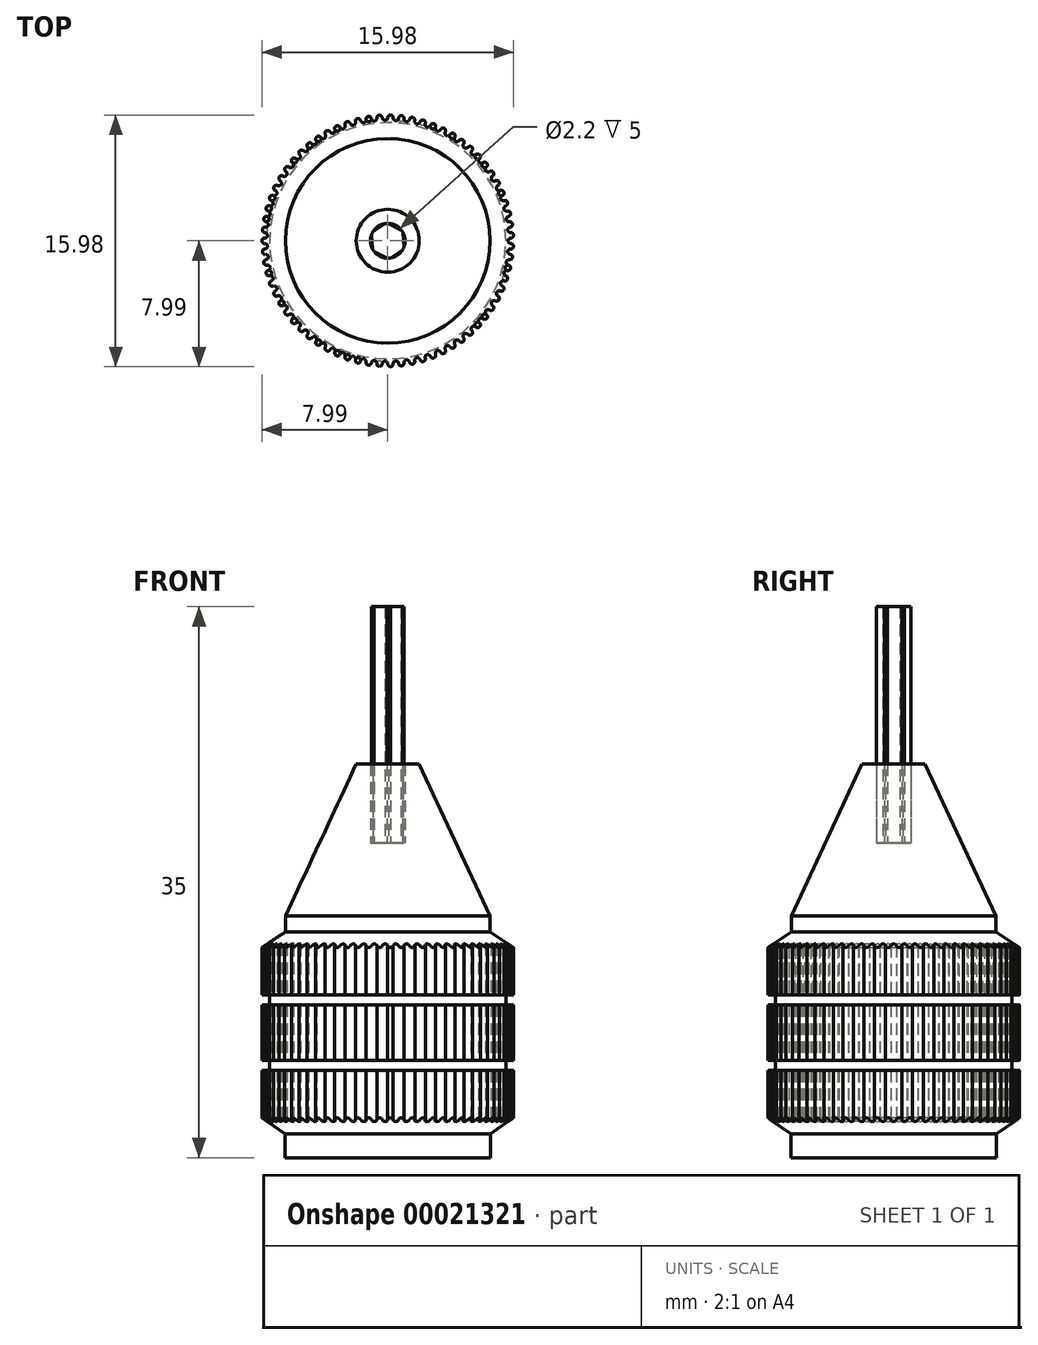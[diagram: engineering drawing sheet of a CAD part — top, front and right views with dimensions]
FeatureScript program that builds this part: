
annotation { "Feature Type Name" : "Feature", "Feature Type Description" : "" }
export const myFeature = defineFeature(function(context is Context, id is Id, definition is map)
    precondition{}
    {
        {
            var Q0;
            Q0=qCreatedBy(makeId("Front.planeOp"),FACE);
            var sketch = newSketch(context, id + "F0", { "sketchPlane" : qUnion([Q0])});
            skLineSegment(sketch, "E0", {"start": v(0, 0) * mm, "end": v(0, 25) * mm, "construction": true});
            skLineSegment(sketch, "E1", {"start": v(0, 0) * mm, "end": v(6.53, 0) * mm});
            skLineSegment(sketch, "E2", {"start": v(6.53, 0) * mm, "end": v(6.53, 1.5) * mm});
            skLineSegment(sketch, "E3", {"start": v(6.53, 1.5) * mm, "end": v(8, 2.54) * mm});
            skLineSegment(sketch, "E4", {"start": v(8, 2.54) * mm, "end": v(8, 13.34) * mm, "construction": true});
            skLineSegment(sketch, "E5", {"start": v(8, 13.34) * mm, "end": v(6.5, 14.34) * mm});
            skLineSegment(sketch, "E6", {"start": v(6.5, 14.34) * mm, "end": v(6.5, 15.34) * mm});
            skLineSegment(sketch, "E7", {"start": v(2, 25) * mm, "end": v(6.5, 15.34) * mm});
            skLineSegment(sketch, "E8", {"start": v(1.1, 25) * mm, "end": v(1.1, 20) * mm});
            skLineSegment(sketch, "E9", {"start": v(1.1, 20) * mm, "end": v(0, 20) * mm});
            skLineSegment(sketch, "E10", {"start": v(1.1, 25) * mm, "end": v(2, 25) * mm});
            skLineSegment(sketch, "E11", {"start": v(8, 13.34) * mm, "end": v(8, 10.34) * mm});
            skLineSegment(sketch, "E12", {"start": v(8, 10.34) * mm, "end": v(7.5, 10.34) * mm});
            skLineSegment(sketch, "E13", {"start": v(7.5, 10.34) * mm, "end": v(7.5, 9.69) * mm});
            skLineSegment(sketch, "E14", {"start": v(7.5, 9.69) * mm, "end": v(8, 9.69) * mm});
            skLineSegment(sketch, "E15", {"start": v(8, 9.69) * mm, "end": v(8, 6.19) * mm});
            skLineSegment(sketch, "E16", {"start": v(8, 6.19) * mm, "end": v(7.5, 6.19) * mm});
            skLineSegment(sketch, "E17", {"start": v(7.5, 6.19) * mm, "end": v(7.5, 5.54) * mm});
            skLineSegment(sketch, "E18", {"start": v(7.5, 5.54) * mm, "end": v(8, 5.54) * mm});
            skLineSegment(sketch, "E19", {"start": v(8, 5.54) * mm, "end": v(8, 2.54) * mm});
            skLineSegment(sketch, "E20", {"start": v(0, 20) * mm, "end": v(0, 0) * mm});
            skSolve(sketch);
        }
        {
            var Q0;
            Q0=qSketchRegion(id+"F0",true);
            var Q1;
            Q1=sQuery(id+"F0.wireOp",EDGE,"E7");
            var Q2;
            Q2=sQuery(id+"F0.wireOp",EDGE,"E5");
            var Q3;
            Q3=sQuery(id+"F0.wireOp",EDGE,"E6");
            var Q4;
            Q4=sQuery(id+"F0.wireOp",EDGE,"E3");
            var Q5;
            Q5=sQuery(id+"F0.wireOp",EDGE,"E2");
            var Q6;
            Q6=sQuery(id+"F0.wireOp",EDGE,"E1");
            var Q7;
            Q7=sQuery(id+"F0.wireOp",EDGE,"E8");
            var Q8;
            Q8=sQuery(id+"F0.wireOp",EDGE,"E9");
            var Q9;
            Q9=sQuery(id+"F0.wireOp",EDGE,"E10");
            var Q10;
            Q10=sQuery(id+"F0.wireOp",EDGE,"E13");
            var Q11;
            Q11=sQuery(id+"F0.wireOp",EDGE,"E12");
            var Q12;
            Q12=sQuery(id+"F0.wireOp",EDGE,"E14");
            var Q13;
            Q13=sQuery(id+"F0.wireOp",EDGE,"E11");
            var Q14;
            Q14=sQuery(id+"F0.wireOp",EDGE,"E15");
            var Q15;
            Q15=sQuery(id+"F0.wireOp",EDGE,"E17");
            var Q16;
            Q16=sQuery(id+"F0.wireOp",EDGE,"E16");
            var Q17;
            Q17=sQuery(id+"F0.wireOp",EDGE,"E18");
            var Q18;
            Q18=sQuery(id+"F0.wireOp",EDGE,"E19");
            var Q19;
            Q19=sQuery(id+"F0.wireOp",EDGE,"E0");
            revolve(context, id + "F1", {"entities" : qUnion([Q0]), "surfaceEntities" : qUnion([Q1, Q2, Q3, Q4, Q5, Q6, Q7, Q8, Q9, Q10, Q11, Q12, Q13, Q14, Q15, Q16, Q17, Q18]), "axis" : qUnion([Q19]), "revolveType" : RevolveType.ONE_DIRECTION, "angle" : 360 * degree});
        }
        {
            var Q0;
            Q0=makeQuery(id+"F1.opRevolve","SWEPT_FACE",FACE,{"disambiguationData":[OSD([sQuery(id+"F0.wireOp",EDGE,"E10")])]});
            var sketch = newSketch(context, id + "F2", { "sketchPlane" : qUnion([Q0])});
            skCircle(sketch, "E21.cCircle", {"center": v(0, 0) * mm, "radius": 1 * mm, "construction": true});
            skLineSegment(sketch, "E21.0", {"start": v(1.03, -0.52) * mm, "end": v(0.06, -1.15) * mm});
            skLineSegment(sketch, "E21.1", {"start": v(0.06, -1.15) * mm, "end": v(-0.97, -0.63) * mm});
            skLineSegment(sketch, "E21.2", {"start": v(-0.97, -0.63) * mm, "end": v(-1.03, 0.52) * mm});
            skLineSegment(sketch, "E21.3", {"start": v(-1.03, 0.52) * mm, "end": v(-0.06, 1.15) * mm});
            skLineSegment(sketch, "E21.4", {"start": v(-0.06, 1.15) * mm, "end": v(0.97, 0.63) * mm});
            skLineSegment(sketch, "E21.5", {"start": v(0.97, 0.63) * mm, "end": v(1.03, -0.52) * mm});
            skPoint(sketch, "E21.0.midPoint", {"position": v(0.55, -0.84) * mm});
            skSolve(sketch);
        }
        {
            var Q0;
            {var subQ0=makeQuery(id+"F1.opRevolve","SWEPT_EDGE",EDGE,{"disambiguationData":[OSD([sQuery(id+"F0.wireOp",VERTEX,"E10.start")])]});var subQ7=sQuery(id+"F2.wireOp",EDGE,"E21.0");var subQ13=makeQuery(id+"F2.imprint","INTERSECT",VERTEX,{"disambiguationData":[OD(0.0)],"derivedFrom":[subQ0,subQ7]});Q0=makeQuery(id+"F2.imprint","IMPRINT",FACE,{"disambiguationData":[TD([[makeQuery(id+"F2.imprint","IMPRINT",EDGE,{"disambiguationData":[TD([[subQ13,-1.0]])],"derivedFrom":subQ7}),-1.0]])]});}
            extrude(context, id + "F3", {"entities" : qUnion([Q0]), "depth" : 10 * mm, "hasSecondDirection" : true, "secondDirectionOppositeDirection" : true, "secondDirectionDepth" : 5 * mm});
        }
        {
            var Q0;
            Q0=qCreatedBy(makeId("Top.planeOp"),FACE);
            var sketch = newSketch(context, id + "F4", { "sketchPlane" : qUnion([Q0])});
            skLineSegment(sketch, "E22", {"start": v(0, 7.82) * mm, "end": v(0, 0) * mm, "construction": true});
            skLineSegment(sketch, "E23", {"start": v(0, 0) * mm, "end": v(0.7, 7.79) * mm, "construction": true});
            skArc(sketch, "E24", {"start": v(0.35, 7.81) * mm, "mid": v(0.18, 8) * mm, "end": v(0, 7.82) * mm});
            skArc(sketch, "E25", {"start": v(0.35, 7.81) * mm, "mid": v(0.5, 7.63) * mm, "end": v(0.7, 7.79) * mm});
            skArc(sketch, "E26", {"start": v(0.7, 7.79) * mm, "mid": v(0.35, 7.81) * mm, "end": v(0, 7.82) * mm, "construction": true});
            skCircle(sketch, "E27", {"center": v(0, 0) * mm, "radius": 8.29 * mm});
            skCircle(sketch, "E28", {"center": v(0, 0) * mm, "radius": 8 * mm, "construction": true});
            skArc(sketch, "E29.1.0", {"start": v(1.03, 7.75) * mm, "mid": v(1.18, 7.56) * mm, "end": v(1.38, 7.7) * mm});
            skArc(sketch, "E29.1.1", {"start": v(1.03, 7.75) * mm, "mid": v(0.88, 7.94) * mm, "end": v(0.7, 7.79) * mm});
            skArc(sketch, "E29.2.0", {"start": v(1.72, 7.63) * mm, "mid": v(1.84, 7.42) * mm, "end": v(2.05, 7.54) * mm});
            skArc(sketch, "E29.2.1", {"start": v(1.72, 7.63) * mm, "mid": v(1.58, 7.84) * mm, "end": v(1.38, 7.7) * mm});
            skArc(sketch, "E29.3.0", {"start": v(2.38, 7.45) * mm, "mid": v(2.5, 7.23) * mm, "end": v(2.71, 7.33) * mm});
            skArc(sketch, "E29.3.1", {"start": v(2.38, 7.45) * mm, "mid": v(2.27, 7.67) * mm, "end": v(2.05, 7.54) * mm});
            skArc(sketch, "E29.4.0", {"start": v(3.03, 7.2) * mm, "mid": v(3.12, 6.98) * mm, "end": v(3.35, 7.07) * mm});
            skArc(sketch, "E29.4.1", {"start": v(3.03, 7.2) * mm, "mid": v(2.94, 7.43) * mm, "end": v(2.71, 7.33) * mm});
            skArc(sketch, "E29.5.0", {"start": v(3.66, 6.91) * mm, "mid": v(3.73, 6.68) * mm, "end": v(3.96, 6.74) * mm});
            skArc(sketch, "E29.5.1", {"start": v(3.66, 6.91) * mm, "mid": v(3.58, 7.15) * mm, "end": v(3.35, 7.07) * mm});
            skArc(sketch, "E29.6.0", {"start": v(4.25, 6.56) * mm, "mid": v(4.3, 6.32) * mm, "end": v(4.54, 6.37) * mm});
            skArc(sketch, "E29.6.1", {"start": v(4.25, 6.56) * mm, "mid": v(4.2, 6.8) * mm, "end": v(3.96, 6.74) * mm});
            skArc(sketch, "E29.7.0", {"start": v(4.82, 6.16) * mm, "mid": v(4.84, 5.92) * mm, "end": v(5.08, 5.94) * mm});
            skArc(sketch, "E29.7.1", {"start": v(4.82, 6.16) * mm, "mid": v(4.78, 6.4) * mm, "end": v(4.54, 6.37) * mm});
            skArc(sketch, "E29.8.0", {"start": v(5.34, 5.7) * mm, "mid": v(5.35, 5.47) * mm, "end": v(5.59, 5.47) * mm});
            skArc(sketch, "E29.8.1", {"start": v(5.34, 5.7) * mm, "mid": v(5.33, 5.96) * mm, "end": v(5.08, 5.94) * mm});
            skArc(sketch, "E29.9.0", {"start": v(5.83, 5.21) * mm, "mid": v(5.8, 4.97) * mm, "end": v(6.05, 4.95) * mm});
            skArc(sketch, "E29.9.1", {"start": v(5.83, 5.21) * mm, "mid": v(5.84, 5.46) * mm, "end": v(5.59, 5.47) * mm});
            skArc(sketch, "E29.10.0", {"start": v(6.26, 4.68) * mm, "mid": v(6.23, 4.44) * mm, "end": v(6.46, 4.4) * mm});
            skArc(sketch, "E29.10.1", {"start": v(6.26, 4.68) * mm, "mid": v(6.3, 4.92) * mm, "end": v(6.05, 4.95) * mm});
            skArc(sketch, "E29.11.0", {"start": v(6.65, 4.1) * mm, "mid": v(6.6, 3.87) * mm, "end": v(6.83, 3.8) * mm});
            skArc(sketch, "E29.11.1", {"start": v(6.65, 4.1) * mm, "mid": v(6.7, 4.35) * mm, "end": v(6.46, 4.4) * mm});
            skArc(sketch, "E29.12.0", {"start": v(6.99, 3.5) * mm, "mid": v(6.91, 3.27) * mm, "end": v(7.14, 3.2) * mm});
            skArc(sketch, "E29.12.1", {"start": v(6.99, 3.5) * mm, "mid": v(7.07, 3.74) * mm, "end": v(6.83, 3.8) * mm});
            skArc(sketch, "E29.13.0", {"start": v(7.27, 2.87) * mm, "mid": v(7.17, 2.65) * mm, "end": v(7.4, 2.55) * mm});
            skArc(sketch, "E29.13.1", {"start": v(7.27, 2.87) * mm, "mid": v(7.37, 3.1) * mm, "end": v(7.14, 3.2) * mm});
            skArc(sketch, "E29.14.0", {"start": v(7.5, 2.22) * mm, "mid": v(7.38, 2) * mm, "end": v(7.59, 1.88) * mm});
            skArc(sketch, "E29.14.1", {"start": v(7.5, 2.22) * mm, "mid": v(7.61, 2.44) * mm, "end": v(7.4, 2.55) * mm});
            skArc(sketch, "E29.15.0", {"start": v(7.66, 1.55) * mm, "mid": v(7.53, 1.35) * mm, "end": v(7.73, 1.2) * mm});
            skArc(sketch, "E29.15.1", {"start": v(7.66, 1.55) * mm, "mid": v(7.8, 1.75) * mm, "end": v(7.59, 1.88) * mm});
            skArc(sketch, "E29.16.0", {"start": v(7.77, 0.86) * mm, "mid": v(7.62, 0.68) * mm, "end": v(7.8, 0.52) * mm});
            skArc(sketch, "E29.16.1", {"start": v(7.77, 0.86) * mm, "mid": v(7.92, 1.06) * mm, "end": v(7.73, 1.2) * mm});
            skArc(sketch, "E29.17.0", {"start": v(7.82, 0.17) * mm, "mid": v(7.65, 0) * mm, "end": v(7.82, -0.17) * mm});
            skArc(sketch, "E29.17.1", {"start": v(7.82, 0.17) * mm, "mid": v(7.99, 0.35) * mm, "end": v(7.8, 0.52) * mm});
            skArc(sketch, "E29.18.0", {"start": v(7.8, -0.52) * mm, "mid": v(7.62, -0.68) * mm, "end": v(7.77, -0.86) * mm});
            skArc(sketch, "E29.18.1", {"start": v(7.8, -0.52) * mm, "mid": v(7.99, -0.35) * mm, "end": v(7.82, -0.17) * mm});
            skArc(sketch, "E29.19.0", {"start": v(7.73, -1.2) * mm, "mid": v(7.53, -1.35) * mm, "end": v(7.66, -1.55) * mm});
            skArc(sketch, "E29.19.1", {"start": v(7.73, -1.2) * mm, "mid": v(7.92, -1.06) * mm, "end": v(7.77, -0.86) * mm});
            skArc(sketch, "E29.20.0", {"start": v(7.59, -1.88) * mm, "mid": v(7.38, -2) * mm, "end": v(7.5, -2.22) * mm});
            skArc(sketch, "E29.20.1", {"start": v(7.59, -1.88) * mm, "mid": v(7.8, -1.75) * mm, "end": v(7.66, -1.55) * mm});
            skArc(sketch, "E29.21.0", {"start": v(7.4, -2.55) * mm, "mid": v(7.17, -2.65) * mm, "end": v(7.27, -2.87) * mm});
            skArc(sketch, "E29.21.1", {"start": v(7.4, -2.55) * mm, "mid": v(7.61, -2.44) * mm, "end": v(7.5, -2.22) * mm});
            skArc(sketch, "E29.22.0", {"start": v(7.14, -3.2) * mm, "mid": v(6.91, -3.27) * mm, "end": v(6.99, -3.5) * mm});
            skArc(sketch, "E29.22.1", {"start": v(7.14, -3.2) * mm, "mid": v(7.37, -3.1) * mm, "end": v(7.27, -2.87) * mm});
            skArc(sketch, "E29.23.0", {"start": v(6.83, -3.8) * mm, "mid": v(6.6, -3.87) * mm, "end": v(6.65, -4.1) * mm});
            skArc(sketch, "E29.23.1", {"start": v(6.83, -3.8) * mm, "mid": v(7.07, -3.74) * mm, "end": v(6.99, -3.5) * mm});
            skArc(sketch, "E29.24.0", {"start": v(6.46, -4.4) * mm, "mid": v(6.23, -4.44) * mm, "end": v(6.26, -4.68) * mm});
            skArc(sketch, "E29.24.1", {"start": v(6.46, -4.4) * mm, "mid": v(6.7, -4.35) * mm, "end": v(6.65, -4.1) * mm});
            skArc(sketch, "E29.25.0", {"start": v(6.05, -4.95) * mm, "mid": v(5.8, -4.97) * mm, "end": v(5.83, -5.21) * mm});
            skArc(sketch, "E29.25.1", {"start": v(6.05, -4.95) * mm, "mid": v(6.3, -4.92) * mm, "end": v(6.26, -4.68) * mm});
            skArc(sketch, "E29.26.0", {"start": v(5.59, -5.47) * mm, "mid": v(5.35, -5.47) * mm, "end": v(5.34, -5.7) * mm});
            skArc(sketch, "E29.26.1", {"start": v(5.59, -5.47) * mm, "mid": v(5.84, -5.46) * mm, "end": v(5.83, -5.21) * mm});
            skArc(sketch, "E29.27.0", {"start": v(5.08, -5.94) * mm, "mid": v(4.84, -5.92) * mm, "end": v(4.82, -6.16) * mm});
            skArc(sketch, "E29.27.1", {"start": v(5.08, -5.94) * mm, "mid": v(5.33, -5.96) * mm, "end": v(5.34, -5.7) * mm});
            skArc(sketch, "E29.28.0", {"start": v(4.54, -6.37) * mm, "mid": v(4.3, -6.32) * mm, "end": v(4.25, -6.56) * mm});
            skArc(sketch, "E29.28.1", {"start": v(4.54, -6.37) * mm, "mid": v(4.78, -6.4) * mm, "end": v(4.82, -6.16) * mm});
            skArc(sketch, "E29.29.0", {"start": v(3.96, -6.74) * mm, "mid": v(3.73, -6.68) * mm, "end": v(3.66, -6.91) * mm});
            skArc(sketch, "E29.29.1", {"start": v(3.96, -6.74) * mm, "mid": v(4.2, -6.8) * mm, "end": v(4.25, -6.56) * mm});
            skArc(sketch, "E29.30.0", {"start": v(3.35, -7.07) * mm, "mid": v(3.12, -6.98) * mm, "end": v(3.03, -7.2) * mm});
            skArc(sketch, "E29.30.1", {"start": v(3.35, -7.07) * mm, "mid": v(3.58, -7.15) * mm, "end": v(3.66, -6.91) * mm});
            skArc(sketch, "E29.31.0", {"start": v(2.71, -7.33) * mm, "mid": v(2.5, -7.23) * mm, "end": v(2.38, -7.45) * mm});
            skArc(sketch, "E29.31.1", {"start": v(2.71, -7.33) * mm, "mid": v(2.94, -7.43) * mm, "end": v(3.03, -7.2) * mm});
            skArc(sketch, "E29.32.0", {"start": v(2.05, -7.54) * mm, "mid": v(1.84, -7.42) * mm, "end": v(1.72, -7.63) * mm});
            skArc(sketch, "E29.32.1", {"start": v(2.05, -7.54) * mm, "mid": v(2.27, -7.67) * mm, "end": v(2.38, -7.45) * mm});
            skArc(sketch, "E29.33.0", {"start": v(1.38, -7.7) * mm, "mid": v(1.18, -7.56) * mm, "end": v(1.03, -7.75) * mm});
            skArc(sketch, "E29.33.1", {"start": v(1.38, -7.7) * mm, "mid": v(1.58, -7.84) * mm, "end": v(1.72, -7.63) * mm});
            skArc(sketch, "E29.34.0", {"start": v(0.7, -7.79) * mm, "mid": v(0.5, -7.63) * mm, "end": v(0.35, -7.81) * mm});
            skArc(sketch, "E29.34.1", {"start": v(0.7, -7.79) * mm, "mid": v(0.88, -7.94) * mm, "end": v(1.03, -7.75) * mm});
            skArc(sketch, "E29.35.0", {"start": v(0, -7.82) * mm, "mid": v(-0.17, -7.65) * mm, "end": v(-0.35, -7.81) * mm});
            skArc(sketch, "E29.35.1", {"start": v(0, -7.82) * mm, "mid": v(0.18, -8) * mm, "end": v(0.35, -7.81) * mm});
            skArc(sketch, "E29.36.0", {"start": v(-0.7, -7.79) * mm, "mid": v(-0.84, -7.6) * mm, "end": v(-1.03, -7.75) * mm});
            skArc(sketch, "E29.36.1", {"start": v(-0.7, -7.79) * mm, "mid": v(-0.53, -7.98) * mm, "end": v(-0.35, -7.81) * mm});
            skArc(sketch, "E29.37.0", {"start": v(-1.38, -7.7) * mm, "mid": v(-1.51, -7.5) * mm, "end": v(-1.72, -7.63) * mm});
            skArc(sketch, "E29.37.1", {"start": v(-1.38, -7.7) * mm, "mid": v(-1.23, -7.9) * mm, "end": v(-1.03, -7.75) * mm});
            skArc(sketch, "E29.38.0", {"start": v(-2.05, -7.54) * mm, "mid": v(-2.17, -7.33) * mm, "end": v(-2.38, -7.45) * mm});
            skArc(sketch, "E29.38.1", {"start": v(-2.05, -7.54) * mm, "mid": v(-1.93, -7.76) * mm, "end": v(-1.72, -7.63) * mm});
            skArc(sketch, "E29.39.0", {"start": v(-2.71, -7.33) * mm, "mid": v(-2.8, -7.11) * mm, "end": v(-3.03, -7.2) * mm});
            skArc(sketch, "E29.39.1", {"start": v(-2.71, -7.33) * mm, "mid": v(-2.6, -7.56) * mm, "end": v(-2.38, -7.45) * mm});
            skArc(sketch, "E29.40.0", {"start": v(-3.35, -7.07) * mm, "mid": v(-3.43, -6.84) * mm, "end": v(-3.66, -6.91) * mm});
            skArc(sketch, "E29.40.1", {"start": v(-3.35, -7.07) * mm, "mid": v(-3.26, -7.3) * mm, "end": v(-3.03, -7.2) * mm});
            skArc(sketch, "E29.41.0", {"start": v(-3.96, -6.74) * mm, "mid": v(-4.02, -6.5) * mm, "end": v(-4.25, -6.56) * mm});
            skArc(sketch, "E29.41.1", {"start": v(-3.96, -6.74) * mm, "mid": v(-3.9, -6.98) * mm, "end": v(-3.66, -6.91) * mm});
            skArc(sketch, "E29.42.0", {"start": v(-4.54, -6.37) * mm, "mid": v(-4.58, -6.13) * mm, "end": v(-4.82, -6.16) * mm});
            skArc(sketch, "E29.42.1", {"start": v(-4.54, -6.37) * mm, "mid": v(-4.5, -6.6) * mm, "end": v(-4.25, -6.56) * mm});
            skArc(sketch, "E29.43.0", {"start": v(-5.08, -5.94) * mm, "mid": v(-5.1, -5.7) * mm, "end": v(-5.34, -5.7) * mm});
            skArc(sketch, "E29.43.1", {"start": v(-5.08, -5.94) * mm, "mid": v(-5.06, -6.19) * mm, "end": v(-4.82, -6.16) * mm});
            skArc(sketch, "E29.44.0", {"start": v(-5.59, -5.47) * mm, "mid": v(-5.58, -5.23) * mm, "end": v(-5.83, -5.21) * mm});
            skArc(sketch, "E29.44.1", {"start": v(-5.59, -5.47) * mm, "mid": v(-5.59, -5.71) * mm, "end": v(-5.34, -5.7) * mm});
            skArc(sketch, "E29.45.0", {"start": v(-6.05, -4.95) * mm, "mid": v(-6.02, -4.71) * mm, "end": v(-6.26, -4.68) * mm});
            skArc(sketch, "E29.45.1", {"start": v(-6.05, -4.95) * mm, "mid": v(-6.07, -5.2) * mm, "end": v(-5.83, -5.21) * mm});
            skArc(sketch, "E29.46.0", {"start": v(-6.46, -4.4) * mm, "mid": v(-6.42, -4.16) * mm, "end": v(-6.65, -4.1) * mm});
            skArc(sketch, "E29.46.1", {"start": v(-6.46, -4.4) * mm, "mid": v(-6.5, -4.64) * mm, "end": v(-6.26, -4.68) * mm});
            skArc(sketch, "E29.47.0", {"start": v(-6.83, -3.8) * mm, "mid": v(-6.76, -3.58) * mm, "end": v(-6.99, -3.5) * mm});
            skArc(sketch, "E29.47.1", {"start": v(-6.83, -3.8) * mm, "mid": v(-6.9, -4.05) * mm, "end": v(-6.65, -4.1) * mm});
            skArc(sketch, "E29.48.0", {"start": v(-7.14, -3.2) * mm, "mid": v(-7.05, -2.97) * mm, "end": v(-7.27, -2.87) * mm});
            skArc(sketch, "E29.48.1", {"start": v(-7.14, -3.2) * mm, "mid": v(-7.22, -3.42) * mm, "end": v(-6.99, -3.5) * mm});
            skArc(sketch, "E29.49.0", {"start": v(-7.4, -2.55) * mm, "mid": v(-7.28, -2.33) * mm, "end": v(-7.5, -2.22) * mm});
            skArc(sketch, "E29.49.1", {"start": v(-7.4, -2.55) * mm, "mid": v(-7.5, -2.77) * mm, "end": v(-7.27, -2.87) * mm});
            skArc(sketch, "E29.50.0", {"start": v(-7.59, -1.88) * mm, "mid": v(-7.46, -1.68) * mm, "end": v(-7.66, -1.55) * mm});
            skArc(sketch, "E29.50.1", {"start": v(-7.59, -1.88) * mm, "mid": v(-7.71, -2.1) * mm, "end": v(-7.5, -2.22) * mm});
            skArc(sketch, "E29.51.0", {"start": v(-7.73, -1.2) * mm, "mid": v(-7.58, -1.01) * mm, "end": v(-7.77, -0.86) * mm});
            skArc(sketch, "E29.51.1", {"start": v(-7.73, -1.2) * mm, "mid": v(-7.87, -1.4) * mm, "end": v(-7.66, -1.55) * mm});
            skArc(sketch, "E29.52.0", {"start": v(-7.8, -0.52) * mm, "mid": v(-7.64, -0.34) * mm, "end": v(-7.82, -0.17) * mm});
            skArc(sketch, "E29.52.1", {"start": v(-7.8, -0.52) * mm, "mid": v(-7.96, -0.7) * mm, "end": v(-7.77, -0.86) * mm});
            skArc(sketch, "E29.53.0", {"start": v(-7.82, 0.17) * mm, "mid": v(-7.64, 0.34) * mm, "end": v(-7.8, 0.52) * mm});
            skArc(sketch, "E29.53.1", {"start": v(-7.82, 0.17) * mm, "mid": v(-8, 0) * mm, "end": v(-7.82, -0.17) * mm});
            skArc(sketch, "E29.54.0", {"start": v(-7.77, 0.86) * mm, "mid": v(-7.58, 1.01) * mm, "end": v(-7.73, 1.2) * mm});
            skArc(sketch, "E29.54.1", {"start": v(-7.77, 0.86) * mm, "mid": v(-7.96, 0.7) * mm, "end": v(-7.8, 0.52) * mm});
            skArc(sketch, "E29.55.0", {"start": v(-7.66, 1.55) * mm, "mid": v(-7.46, 1.68) * mm, "end": v(-7.59, 1.88) * mm});
            skArc(sketch, "E29.55.1", {"start": v(-7.66, 1.55) * mm, "mid": v(-7.87, 1.4) * mm, "end": v(-7.73, 1.2) * mm});
            skArc(sketch, "E29.56.0", {"start": v(-7.5, 2.22) * mm, "mid": v(-7.28, 2.33) * mm, "end": v(-7.4, 2.55) * mm});
            skArc(sketch, "E29.56.1", {"start": v(-7.5, 2.22) * mm, "mid": v(-7.71, 2.1) * mm, "end": v(-7.59, 1.88) * mm});
            skArc(sketch, "E29.57.0", {"start": v(-7.27, 2.87) * mm, "mid": v(-7.05, 2.97) * mm, "end": v(-7.14, 3.2) * mm});
            skArc(sketch, "E29.57.1", {"start": v(-7.27, 2.87) * mm, "mid": v(-7.5, 2.77) * mm, "end": v(-7.4, 2.55) * mm});
            skArc(sketch, "E29.58.0", {"start": v(-6.99, 3.5) * mm, "mid": v(-6.76, 3.58) * mm, "end": v(-6.83, 3.8) * mm});
            skArc(sketch, "E29.58.1", {"start": v(-6.99, 3.5) * mm, "mid": v(-7.22, 3.42) * mm, "end": v(-7.14, 3.2) * mm});
            skArc(sketch, "E29.59.0", {"start": v(-6.65, 4.1) * mm, "mid": v(-6.42, 4.16) * mm, "end": v(-6.46, 4.4) * mm});
            skArc(sketch, "E29.59.1", {"start": v(-6.65, 4.1) * mm, "mid": v(-6.9, 4.05) * mm, "end": v(-6.83, 3.8) * mm});
            skArc(sketch, "E29.60.0", {"start": v(-6.26, 4.68) * mm, "mid": v(-6.02, 4.71) * mm, "end": v(-6.05, 4.95) * mm});
            skArc(sketch, "E29.60.1", {"start": v(-6.26, 4.68) * mm, "mid": v(-6.5, 4.64) * mm, "end": v(-6.46, 4.4) * mm});
            skArc(sketch, "E29.61.0", {"start": v(-5.83, 5.21) * mm, "mid": v(-5.58, 5.23) * mm, "end": v(-5.59, 5.47) * mm});
            skArc(sketch, "E29.61.1", {"start": v(-5.83, 5.21) * mm, "mid": v(-6.07, 5.2) * mm, "end": v(-6.05, 4.95) * mm});
            skArc(sketch, "E29.62.0", {"start": v(-5.34, 5.7) * mm, "mid": v(-5.1, 5.7) * mm, "end": v(-5.08, 5.94) * mm});
            skArc(sketch, "E29.62.1", {"start": v(-5.34, 5.7) * mm, "mid": v(-5.59, 5.71) * mm, "end": v(-5.59, 5.47) * mm});
            skArc(sketch, "E29.63.0", {"start": v(-4.82, 6.16) * mm, "mid": v(-4.58, 6.13) * mm, "end": v(-4.54, 6.37) * mm});
            skArc(sketch, "E29.63.1", {"start": v(-4.82, 6.16) * mm, "mid": v(-5.06, 6.19) * mm, "end": v(-5.08, 5.94) * mm});
            skArc(sketch, "E29.64.0", {"start": v(-4.25, 6.56) * mm, "mid": v(-4.02, 6.5) * mm, "end": v(-3.96, 6.74) * mm});
            skArc(sketch, "E29.64.1", {"start": v(-4.25, 6.56) * mm, "mid": v(-4.5, 6.6) * mm, "end": v(-4.54, 6.37) * mm});
            skArc(sketch, "E29.65.0", {"start": v(-3.66, 6.91) * mm, "mid": v(-3.43, 6.84) * mm, "end": v(-3.35, 7.07) * mm});
            skArc(sketch, "E29.65.1", {"start": v(-3.66, 6.91) * mm, "mid": v(-3.9, 6.98) * mm, "end": v(-3.96, 6.74) * mm});
            skArc(sketch, "E29.66.0", {"start": v(-3.03, 7.2) * mm, "mid": v(-2.8, 7.11) * mm, "end": v(-2.71, 7.33) * mm});
            skArc(sketch, "E29.66.1", {"start": v(-3.03, 7.2) * mm, "mid": v(-3.26, 7.3) * mm, "end": v(-3.35, 7.07) * mm});
            skArc(sketch, "E29.67.0", {"start": v(-2.38, 7.45) * mm, "mid": v(-2.17, 7.33) * mm, "end": v(-2.05, 7.54) * mm});
            skArc(sketch, "E29.67.1", {"start": v(-2.38, 7.45) * mm, "mid": v(-2.6, 7.56) * mm, "end": v(-2.71, 7.33) * mm});
            skArc(sketch, "E29.68.0", {"start": v(-1.72, 7.63) * mm, "mid": v(-1.51, 7.5) * mm, "end": v(-1.38, 7.7) * mm});
            skArc(sketch, "E29.68.1", {"start": v(-1.72, 7.63) * mm, "mid": v(-1.93, 7.76) * mm, "end": v(-2.05, 7.54) * mm});
            skArc(sketch, "E29.69.0", {"start": v(-1.03, 7.75) * mm, "mid": v(-0.84, 7.6) * mm, "end": v(-0.7, 7.79) * mm});
            skArc(sketch, "E29.69.1", {"start": v(-1.03, 7.75) * mm, "mid": v(-1.23, 7.9) * mm, "end": v(-1.38, 7.7) * mm});
            skArc(sketch, "E29.70.0", {"start": v(-0.35, 7.81) * mm, "mid": v(-0.17, 7.65) * mm, "end": v(0, 7.82) * mm});
            skArc(sketch, "E29.70.1", {"start": v(-0.35, 7.81) * mm, "mid": v(-0.53, 7.98) * mm, "end": v(-0.7, 7.79) * mm});
            skLineSegment(sketch, "E29.anchor1", {"start": v(0, 0) * mm, "end": v(0, 7.82) * mm, "construction": true});
            skLineSegment(sketch, "E29.anchor2", {"start": v(0, 0) * mm, "end": v(0, 7.82) * mm, "construction": true});
            skSolve(sketch);
        }
        {
            var Q0;
            Q0=makeQuery(id+"F4.imprint","IMPRINT",FACE,{"disambiguationData":[TD([[makeQuery(id+"F4.imprint","IMPRINT",EDGE,{"derivedFrom":sQuery(id+"F4.wireOp",EDGE,"E27")}),1.0]])]});
            extrude(context, id + "F5", {"entities" : qUnion([Q0]), "operationType" : NewBodyOperationType.REMOVE, "depth" : 25 * mm});
        }
    });
